# Revit family: Legrand Distribution enclosure XL³ 4000 external cables sleeves
name_source: partatom
category: Equipement électrique
units: mm (PartAtom-declared; Revit-internal decimal feet)

## family parameters
Basée sur le plan de construction = Non
Configuration du panneau = Deux colonnes, circuits au sein
Cote de connecteur circulaire = Utiliser le diamètre
Couper avec des vides une fois chargée = Non
Numéro OmniClass = 23.80.30.11.17
Partagée = Non
Point de calcul de pièce = Non
Titre OmniClass = Distribution Boards and Control Panels
Toujours verticalement = Oui
Type d'élément = Tableau de raccordement

## types (6) — shared parameters
Fabricant = Legrand
Finish = Epoxipolyester paint deposited by electrostatic powder
General Conditions of Use = https://export.legrand.com
ICW (until) = 110
IK with door = 08
IK without door = 07
IN max (A) = 4000
IP with door = 55
IP without door = 30
Material = Steel
Modèle = XL³ 4000
RAL = 7035
URL = https://www.legrand.fr
width (mm) = 475 mm  [stored 1.5584 ft]
zero-valued in all types: Elévation par défaut

## per-type parameters (varying)
| type | depth (mm) | height (mm) |
| 020501-020500-020511-020554 | 475 mm  [stored 1.5584 ft] | 2000 mm  [stored 6.56168 ft] |
| 020501-020850-020511-020861 | 475 mm  [stored 1.5584 ft] | 2200 mm |
| 020502-020500-020514-020554 | 725 mm  [stored 2.37861 ft] | 2000 mm  [stored 6.56168 ft] |
| 020502-020850-020514-020861 | 725 mm  [stored 2.37861 ft] | 2200 mm |
| 020503-020500-020517-020554 | 975 mm  [stored 3.19882 ft] | 2000 mm  [stored 6.56168 ft] |
| 020503-020850-020517-020861 | 975 mm  [stored 3.19882 ft] | 2200 mm |

note: [stored X ft] marks values corroborated as IEEE doubles in the binary element streams (Revit-internal decimal feet)
